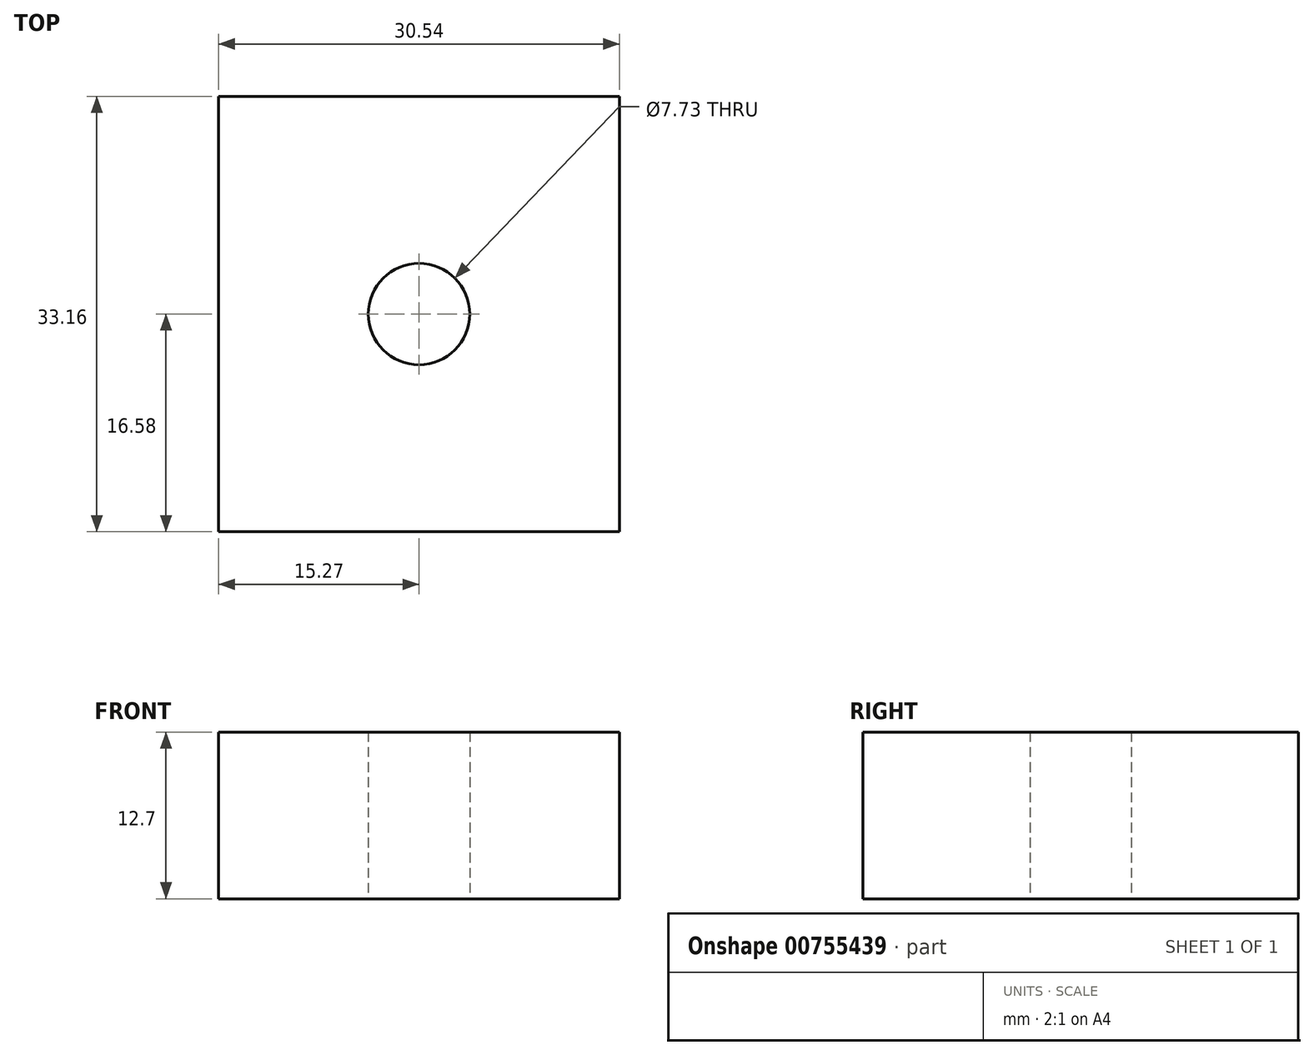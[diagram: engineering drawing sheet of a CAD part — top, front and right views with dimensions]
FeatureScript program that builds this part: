
annotation { "Feature Type Name" : "Feature", "Feature Type Description" : "" }
export const myFeature = defineFeature(function(context is Context, id is Id, definition is map)
    precondition{}
    {
        {
            var Q0;
            Q0=qCreatedBy(makeId("Top.planeOp"),FACE);
            var sketch = newSketch(context, id + "F0", { "sketchPlane" : qUnion([Q0])});
            skLineSegment(sketch, "E0.bottom", {"start": v(-15.27, 16.58) * mm, "end": v(15.27, 16.58) * mm});
            skLineSegment(sketch, "E0.top", {"start": v(-15.27, -16.58) * mm, "end": v(15.27, -16.58) * mm});
            skLineSegment(sketch, "E0.left", {"start": v(-15.27, 16.58) * mm, "end": v(-15.27, -16.58) * mm});
            skLineSegment(sketch, "E0.right", {"start": v(15.27, 16.58) * mm, "end": v(15.27, -16.58) * mm});
            skPoint(sketch, "E0.middle", {"position": v(0, 0) * mm});
            skSolve(sketch);
        }
        {
            var Q0;
            Q0 = qSketchRegion(id + "F0", true);
            var sketch = newSketch(context, id + "F1", { "sketchPlane" : qUnion([Q0])});
            skLineSegment(sketch, "E1.bottom", {"start": v(-8.23, 6.43) * mm, "end": v(8.23, 6.43) * mm});
            skLineSegment(sketch, "E1.top", {"start": v(-8.23, -6.43) * mm, "end": v(8.23, -6.43) * mm});
            skLineSegment(sketch, "E1.left", {"start": v(-8.23, 6.43) * mm, "end": v(-8.23, -6.43) * mm});
            skLineSegment(sketch, "E1.right", {"start": v(8.23, 6.43) * mm, "end": v(8.23, -6.43) * mm});
            skPoint(sketch, "E1.middle", {"position": v(0, 0) * mm});
            skCircle(sketch, "E2", {"center": v(0, 0) * mm, "radius": 3.86 * mm});
            skSolve(sketch);
        }
        {
            var Q0;
            Q0 = qSketchRegion(id + "F1", true);
            var Q1;
            Q1=makeQuery(id+"F1.imprint","IMPRINT",FACE,{"disambiguationData":[TD([[makeQuery(id+"F1.imprint","IMPRINT",EDGE,{"derivedFrom":sQuery(id+"F1.wireOp",EDGE,"E1.bottom")}),1.0]])]});
            extrude(context, id + "F2", {"entities" : qUnion([Q0, Q1]), "depth" : 12.7 * mm, "offsetDistance" : 25.4 * mm});
        }
    });
